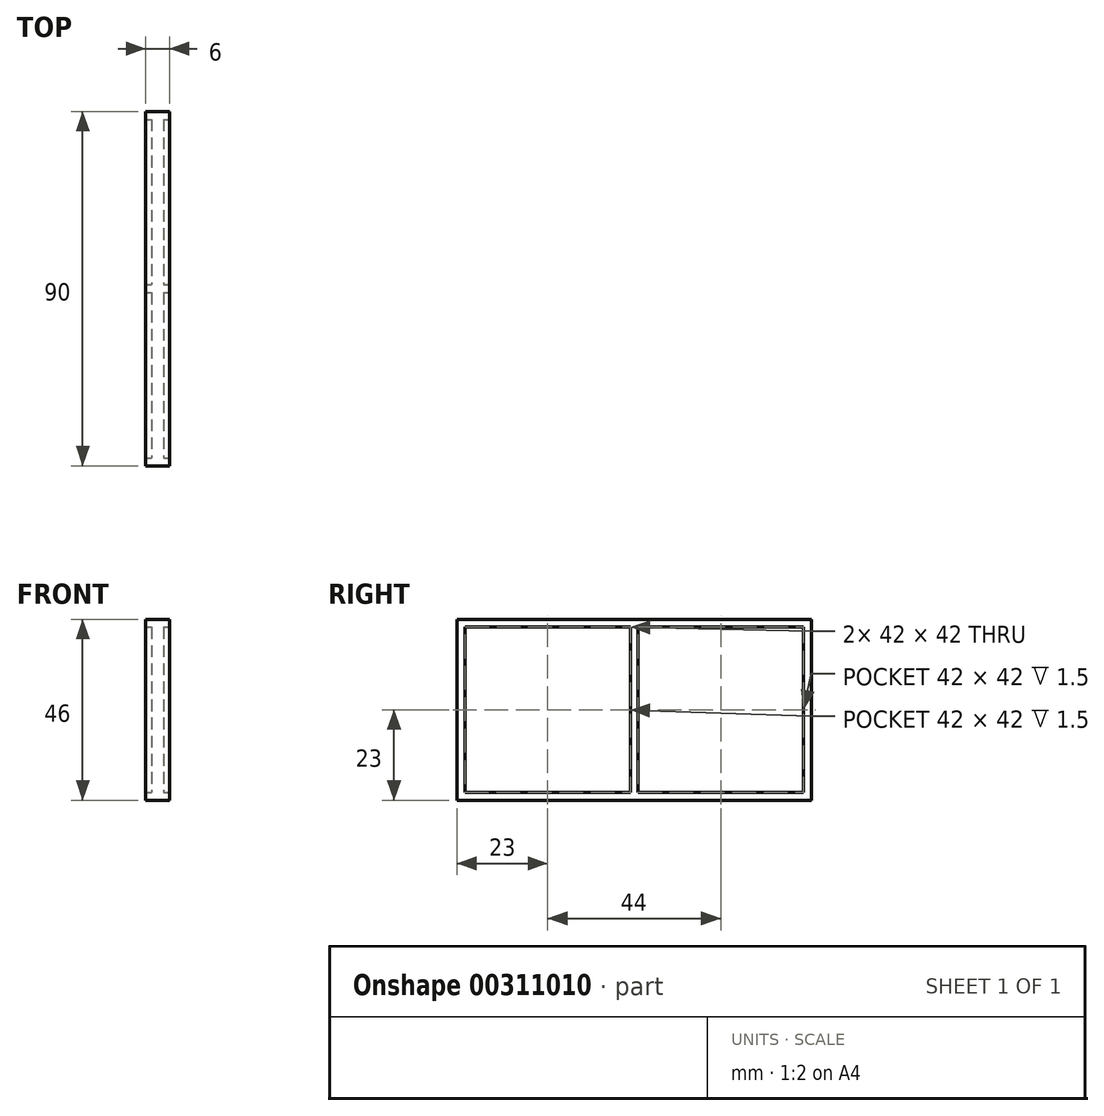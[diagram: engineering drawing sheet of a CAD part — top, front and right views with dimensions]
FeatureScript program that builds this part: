
annotation { "Feature Type Name" : "Feature", "Feature Type Description" : "" }
export const myFeature = defineFeature(function(context is Context, id is Id, definition is map)
    precondition{}
    {
        {
            var Q0;
            Q0=qCreatedBy(makeId("Right.planeOp"),FACE);
            var sketch = newSketch(context, id + "F0", { "sketchPlane" : qUnion([Q0])});
            skPoint(sketch, "E0.middle", {"position": v(-22, 0) * mm});
            skPoint(sketch, "E1.middle", {"position": v(22, 0) * mm});
            skLineSegment(sketch, "E2.bottom", {"start": v(-45, 23) * mm, "end": v(45, 23) * mm});
            skLineSegment(sketch, "E2.top", {"start": v(-45, -23) * mm, "end": v(45, -23) * mm});
            skLineSegment(sketch, "E2.left", {"start": v(-45, 23) * mm, "end": v(-45, -23) * mm});
            skLineSegment(sketch, "E2.right", {"start": v(45, 23) * mm, "end": v(45, -23) * mm});
            skPoint(sketch, "E2.middle", {"position": v(0, 0) * mm});
            skSolve(sketch);
        }
        {
            var Q0;
            Q0 = qSketchRegion(id + "F0", true);
            extrude(context, id + "F1", {"entities" : qUnion([Q0]), "endBound" : BoundingType.SYMMETRIC, "depth" : 6 * mm});
        }
        {
            var Q0;
            Q0=makeQuery(id+"F1.opExtrude","CAP_FACE",FACE,{"disambiguationData":[OSD([sQuery(id+"F0.wireOp",EDGE,"E2.bottom"),sQuery(id+"F0.wireOp",EDGE,"E2.top"),sQuery(id+"F0.wireOp",EDGE,"E2.left"),sQuery(id+"F0.wireOp",EDGE,"E2.right")])],"isStart":false});
            var sketch = newSketch(context, id + "F2", { "sketchPlane" : qUnion([Q0])});
            skLineSegment(sketch, "E3.bottom", {"start": v(-1, 21) * mm, "end": v(-43, 21) * mm});
            skLineSegment(sketch, "E3.top", {"start": v(-1, -21) * mm, "end": v(-43, -21) * mm});
            skLineSegment(sketch, "E3.left", {"start": v(-1, 21) * mm, "end": v(-1, -21) * mm});
            skLineSegment(sketch, "E3.right", {"start": v(-43, 21) * mm, "end": v(-43, -21) * mm});
            skPoint(sketch, "E3.middle", {"position": v(-22, 0) * mm});
            skLineSegment(sketch, "E4.bottom", {"start": v(43, 21) * mm, "end": v(1, 21) * mm});
            skLineSegment(sketch, "E4.top", {"start": v(43, -21) * mm, "end": v(1, -21) * mm});
            skLineSegment(sketch, "E4.left", {"start": v(43, 21) * mm, "end": v(43, -21) * mm});
            skLineSegment(sketch, "E4.right", {"start": v(1, 21) * mm, "end": v(1, -21) * mm});
            skPoint(sketch, "E4.middle", {"position": v(22, 0) * mm});
            skSolve(sketch);
        }
        {
            var Q0;
            Q0 = qSketchRegion(id + "F2", true);
            extrude(context, id + "F3", {"entities" : qUnion([Q0]), "operationType" : NewBodyOperationType.REMOVE, "oppositeDirection" : true, "depth" : 6 * mm, "hasSecondDirection" : true, "secondDirectionOppositeDirection" : true, "secondDirectionDepth" : 4.5 * mm});
        }
        {
            var Q0;
            Q0 = qSketchRegion(id + "F2", true);
            extrude(context, id + "F4", {"entities" : qUnion([Q0]), "operationType" : NewBodyOperationType.REMOVE, "oppositeDirection" : true, "depth" : 1.5 * mm});
        }
    });
